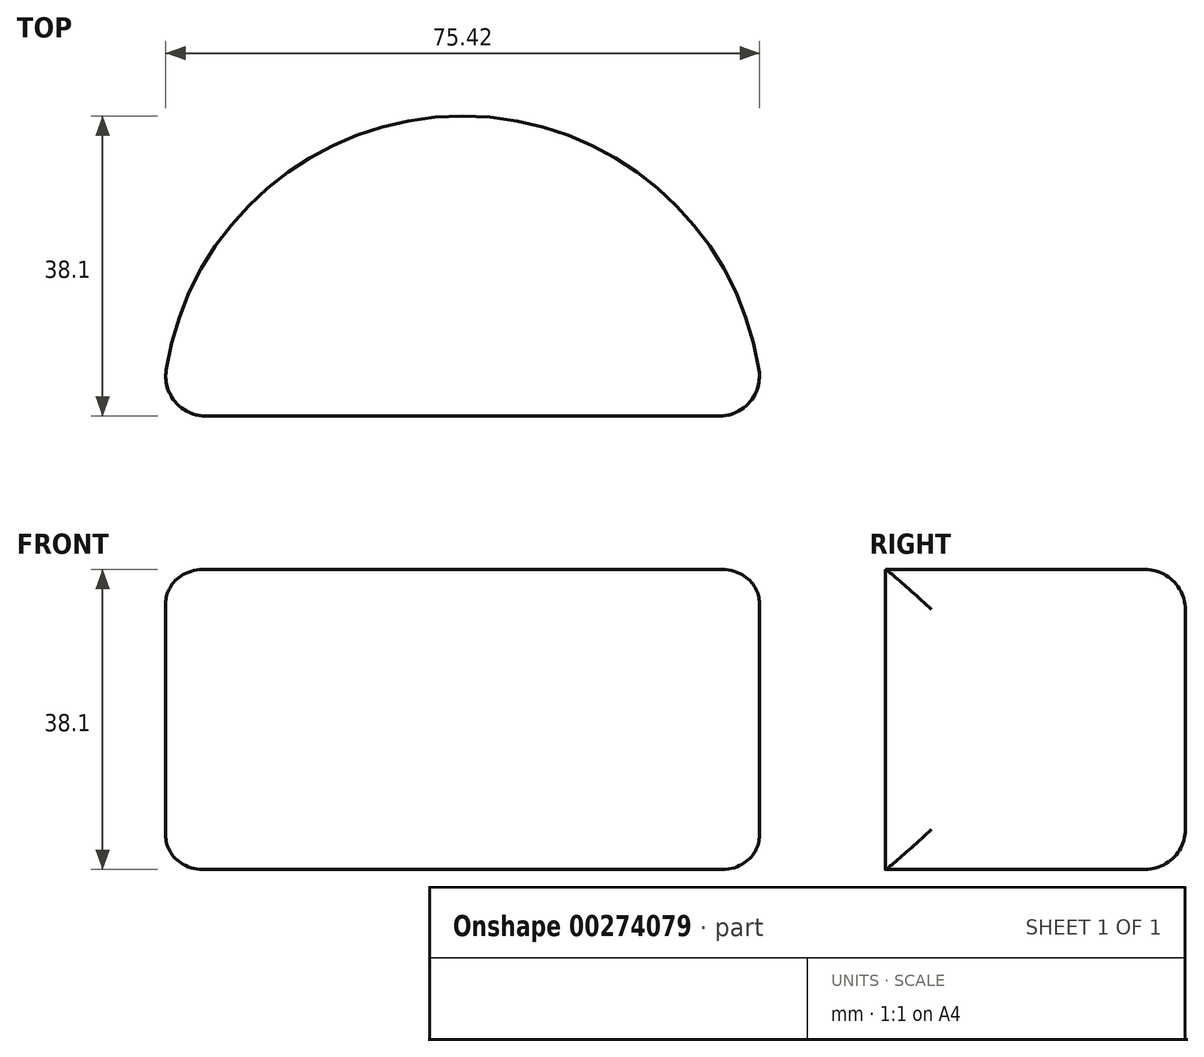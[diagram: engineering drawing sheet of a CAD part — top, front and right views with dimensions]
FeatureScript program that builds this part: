
annotation { "Feature Type Name" : "Feature", "Feature Type Description" : "" }
export const myFeature = defineFeature(function(context is Context, id is Id, definition is map)
    precondition{}
    {
        {
            var Q0;
            Q0=qCreatedBy(makeId("Top.planeOp"),FACE);
            var sketch = newSketch(context, id + "F0", { "sketchPlane" : qUnion([Q0])});
            skArc(sketch, "E0", {"start": v(38.1, 0) * mm, "mid": v(0, 38.1) * mm, "end": v(-38.1, 0) * mm});
            skLineSegment(sketch, "E1", {"start": v(-38.1, 0) * mm, "end": v(38.1, 0) * mm});
            skSolve(sketch);
        }
        {
            var Q0;
            Q0=makeQuery(id+"F0.imprint","IMPRINT",FACE,{"disambiguationData":[TD([[makeQuery(id+"F0.imprint","IMPRINT",EDGE,{"derivedFrom":sQuery(id+"F0.wireOp",EDGE,"E0")}),1.0]])]});
            extrude(context, id + "F1", {"entities" : qUnion([Q0]), "depth" : 38.1 * mm});
        }
        {
            var Q0;
            Q0=makeQuery(id+"F1.opExtrude","CAP_EDGE",EDGE,{"disambiguationData":[OSD([sQuery(id+"F0.wireOp",EDGE,"E0")])],"isStart":false});
            var Q1;
            Q1=makeQuery(id+"F1.opExtrude","SWEPT_FACE",FACE,{"disambiguationData":[OSD([sQuery(id+"F0.wireOp",EDGE,"E0")])]});
            fillet(context, id + "F2", {"entities" : qUnion([Q0, Q1]), "radius" : 5.08 * mm, "tangentPropagation" : true, "allowEdgeOverflow" : false});
        }
    });
